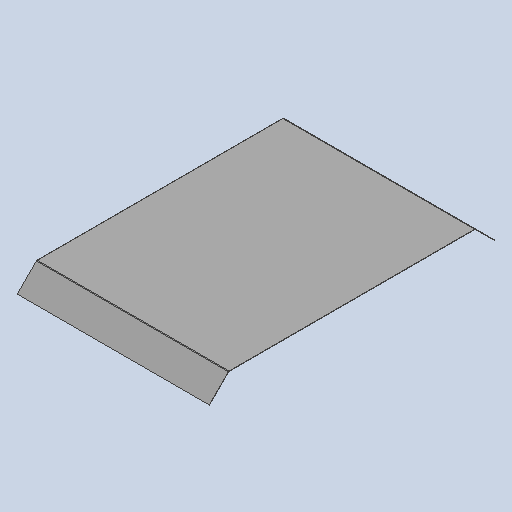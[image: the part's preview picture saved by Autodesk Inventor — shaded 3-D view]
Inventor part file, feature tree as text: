
AUTODESK INVENTOR PART (.ipt)
format: ipt  version: 2025 (Build 290162010, 162A)  size: 248,320 bytes
history: native  units: mm
features: other x5, sheet_metal_op x4, sketch x3
ambient origin geometry x8: Origin, YZ Plane, XZ Plane, XY Plane, X Axis, Y Axis, Z Axis, Center Point
bodies: Solid1 (feature_tree)
feature tree (12):
  sheet_metal_op  "Face1"
  sheet_metal_op  "Flange1"
  other  "Mark1"
  other  "A-Side Definition"
  sketch  "Sketch1"  dims[d0=1479.0mm]
  other  "Plate1"
  sketch  "Sketch2"  dims[d1=1900.0mm]
  other  "Plate2"
  sheet_metal_op  "Bend1"
  sheet_metal_op  "Corner1"
  sketch  "Sketch4"  dims[d2=3.0mm d3=3.0mm d4=1.5mm d5=6.0mm d6=5.0mm d7=212.0mm d8=45.0deg d9=5.0mm d10=12.0mm d11=3.0mm d12=5.0mm d13=200.0mm d14=15.0mm d15=25.0mm d16=25.0mm]
  other  "Definition1"
